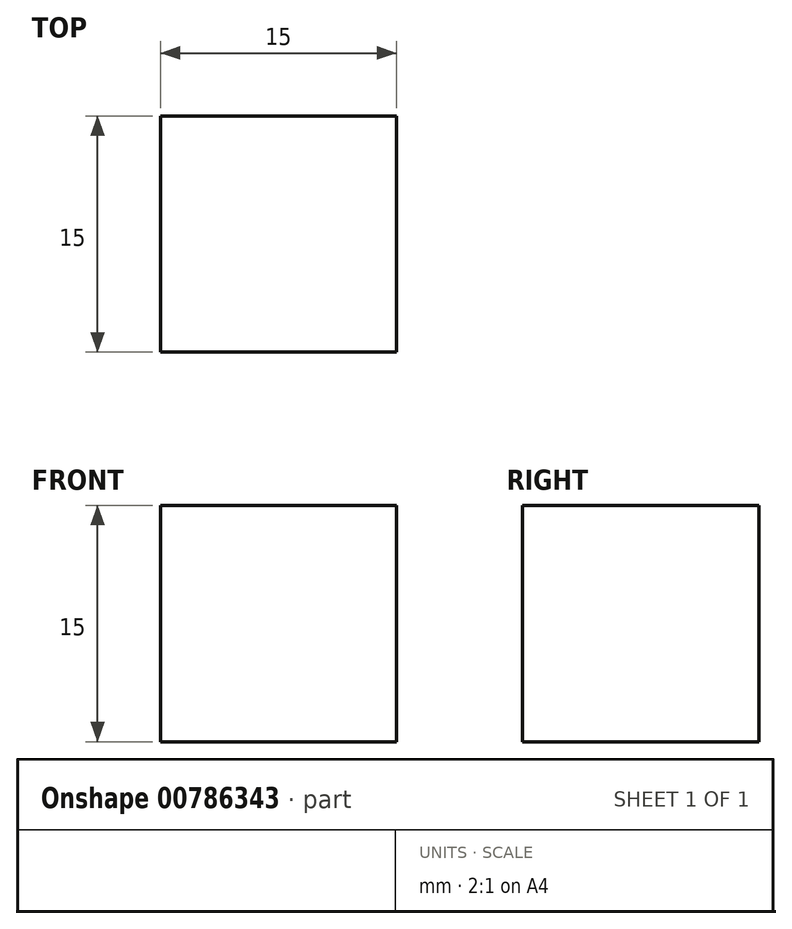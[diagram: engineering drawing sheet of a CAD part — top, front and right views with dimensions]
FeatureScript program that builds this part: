
annotation { "Feature Type Name" : "Feature", "Feature Type Description" : "" }
export const myFeature = defineFeature(function(context is Context, id is Id, definition is map)
    precondition{}
    {
        {
            var Q0;
            Q0=qCreatedBy(makeId("Front.planeOp"),FACE);
            var sketch = newSketch(context, id + "F0", { "sketchPlane" : qUnion([Q0])});
            skLineSegment(sketch, "E0.bottom", {"start": v(0, 0) * mm, "end": v(15, 0) * mm});
            skLineSegment(sketch, "E0.top", {"start": v(0, 15) * mm, "end": v(15, 15) * mm});
            skLineSegment(sketch, "E0.left", {"start": v(0, 0) * mm, "end": v(0, 15) * mm});
            skLineSegment(sketch, "E0.right", {"start": v(15, 0) * mm, "end": v(15, 15) * mm});
            skSolve(sketch);
        }
        {
            var Q0;
            Q0 = qSketchRegion(id + "F0", true);
            extrude(context, id + "F1", {"entities" : qUnion([Q0]), "depth" : 15 * mm, "offsetDistance" : 25 * mm});
        }
    });
